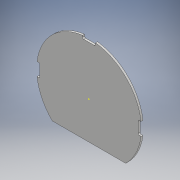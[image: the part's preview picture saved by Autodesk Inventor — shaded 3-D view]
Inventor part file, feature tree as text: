
AUTODESK INVENTOR PART (.ipt)
format: ipt  version: 2017 (Build 210142000, 142)  size: 143,872 bytes
history: native  units: mm
features: sketch x4, extrude x3, fillet x1, projected_geometry x1
ambient origin geometry x8: Origin, YZ Plane, XZ Plane, XY Plane, X Axis, Y Axis, Z Axis, Center Point
bodies: Solide1 (feature_tree)
feature tree (9):
  extrude  "Extrusion1"  Depth=160.0mm
  extrude  "Extrusion2"  Depth=3.0mm TaperAngle=0.0deg
  fillet  "Congé1"  Radius=20.0mm
  sketch  "Esquisse4"
  extrude  "Extrusion4"  Depth=80.0mm
  sketch  "Esquisse1"
  sketch  "Esquisse2"
  sketch  "Esquisse5"
  projected_geometry  "Boucle projetée1"
